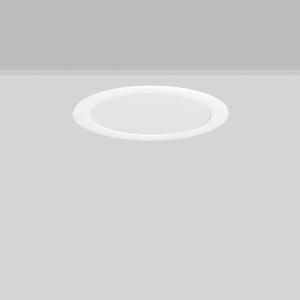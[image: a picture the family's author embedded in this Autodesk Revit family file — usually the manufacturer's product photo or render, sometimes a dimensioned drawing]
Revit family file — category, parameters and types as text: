
# Revit family: toledo_flat_round_e_672226_002_1_04_98b7
name_source: partatom
category: Lighting Fixtures
units: mm (PartAtom-declared; Revit-internal decimal feet)

## family parameters
Cut with Voids When Loaded = No
Host = Face
Light Source = No
Part Type = Normal
Room Calculation Point = No
Round Connector Dimension = Use Diameter
Shared = No

## types (1)
- TOLEDO FLAT round E (1 x LED Modul 840, 2250 lm, 4000)
    Apparent Load = 22 VA
    CIE Flux Codes = 49 80 96 100 100
    Color Rendering = 80
    Color Temperature = 4000
    Default Elevation = 1800 mm
    Description = Series: TOLEDO FLAT round
Ultra thin recessed downlight. For escape route illumination. Housing: die-cast aluminium, powder-coated. Lightguide and diffuser made of non-yellowing plastic (PMMA). Diffuser opal matt plastic. Ceiling installation with spring system. Including separate LED converter with connecting cable 250 mm. Self-contained system with automatic self-test and feedback to the RZB monitoring system MULTIDIGIT. External driver with simple plug-in locking system. 
Colour: white
Diameter: 317 mm
Height: 3 mm
Cut-out diameter: 288 mm
Recess height: 90 mm
Luminaire: recess height: 60-80 mm
Weight: 2.28 kg
Operating mode: maintained power mode
Duration time: 3 h
Lamp: LED
Socket: without socket
Colour temperature: 4000K
Colour rendering index (CRI): 80
System power: 22 W
Rated luminous flux: 2250 lm
Luminous flux, emergency: 440 lm
System power, emergency: -
Control gear: Regulated power supply
Protection class: I
Type of protection: IP 54
    Height = 0 mm  [stored 0 ft]
    Lamp = 1 x LED Modul 840
    Lamp Light Flux = 2250 lm
    Lamp count = 1
    Length = 317 mm
    Lifetime = 50000 h
    Luminous efficacy = 102 lm/W
    Manufacturer = RZB
    ModVariant = No
    Model = 672226.002.1.04
    Mounting Place = Ceiling
    Mounting Type = Recessed
    Number of Poles = 1
    OnlyDefault = Yes
    Power Factor = 1
    Product Name = TOLEDO FLAT round E
    Product group = Recessed downlights
    ProductGroupID = 402
    Protection Class = Protection class I
    Protection Degree = IP 40
    RLX_Detail_Level = 1
    RLX_Emergency_Light_Flux = 440 lm
    RLX_Emergency_Type = 3
    RLX_Emergency_Type_DB = Yes
    RlxData = <blob elided: 31681 chars, md5=9d4b599d>
    Socket = socket
    Standby Power = 0 W
    System Light Flux = 2250 lm
    System Power = 22 W
    Type Comments = Product without accessories
    Type Image = 901484.002.jpg
    URL = http://relux.com
    VarID = ---
    Voltage = 0 V
    Weight = 0.00 kg
    Width = 0 mm  [stored 0 ft]

note: [stored X ft] marks values corroborated as IEEE doubles in the binary element streams (Revit-internal decimal feet)

## geometry (parser evidence)
native form markers: Blend x4, Sweep x11
no freeform markers — native parametric forms only
